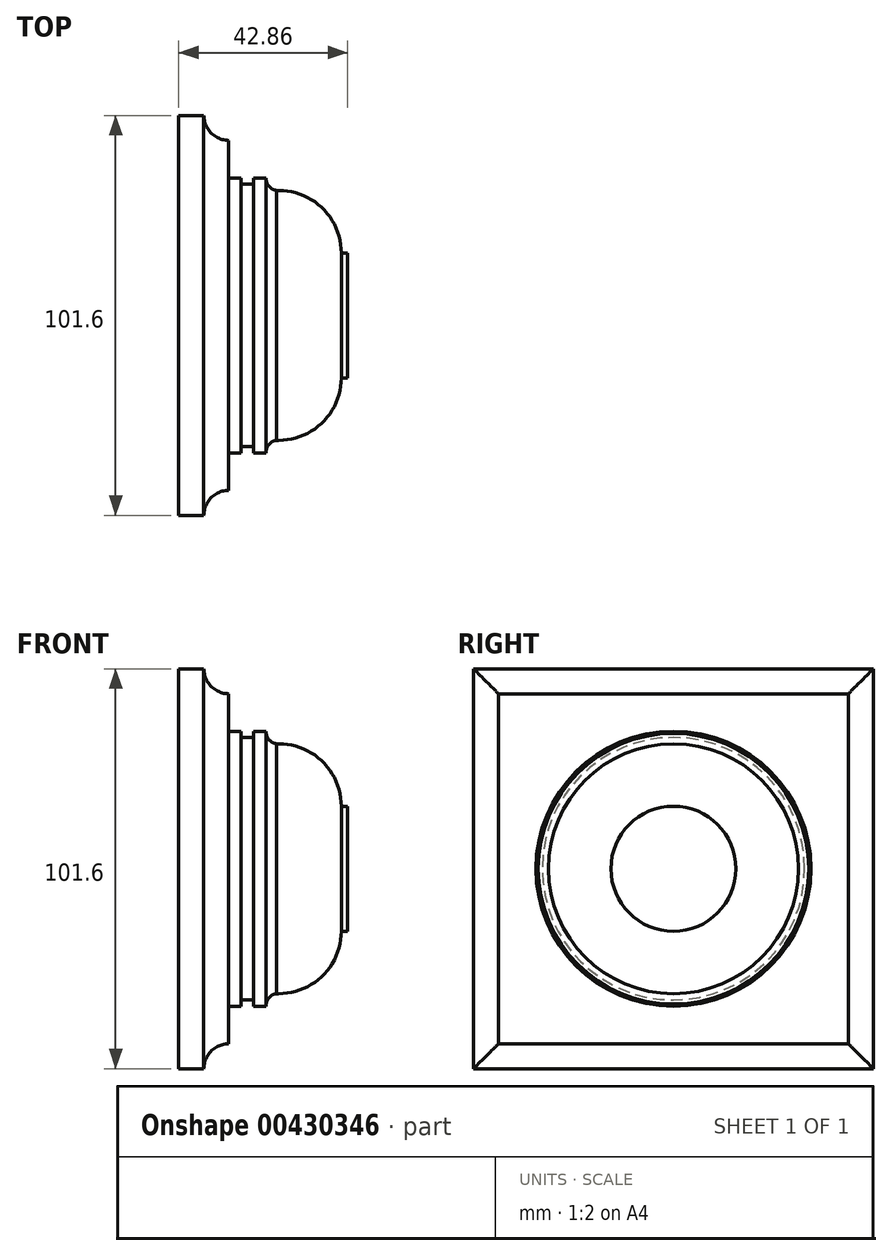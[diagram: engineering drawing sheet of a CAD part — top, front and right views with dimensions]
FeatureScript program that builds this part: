
annotation { "Feature Type Name" : "Feature", "Feature Type Description" : "" }
export const myFeature = defineFeature(function(context is Context, id is Id, definition is map)
    precondition{}
    {
        {
            var Q0;
            Q0=qCreatedBy(makeId("Front.planeOp"),FACE);
            var sketch = newSketch(context, id + "F0", { "sketchPlane" : qUnion([Q0])});
            skLineSegment(sketch, "E0", {"start": v(0, 0) * mm, "end": v(0, 34.93) * mm});
            skLineSegment(sketch, "E1", {"start": v(0, 34.93) * mm, "end": v(3.18, 34.93) * mm});
            skLineSegment(sketch, "E2", {"start": v(3.18, 34.93) * mm, "end": v(3.18, 33.34) * mm});
            skLineSegment(sketch, "E3", {"start": v(3.18, 33.34) * mm, "end": v(6.35, 33.34) * mm});
            skLineSegment(sketch, "E4", {"start": v(6.35, 33.34) * mm, "end": v(6.35, 34.93) * mm});
            skLineSegment(sketch, "E5", {"start": v(6.35, 34.93) * mm, "end": v(9.53, 34.93) * mm});
            skLineSegment(sketch, "E6", {"start": v(9.53, 34.93) * mm, "end": v(9.53, 34.36) * mm});
            skLineSegment(sketch, "E7", {"start": v(12.14, 31.75) * mm, "end": v(12.7, 31.75) * mm});
            skLineSegment(sketch, "E8", {"start": v(12.7, 31.75) * mm, "end": v(12.7, 31.75) * mm});
            skLineSegment(sketch, "E9", {"start": v(28.58, 15.88) * mm, "end": v(28.58, 15.88) * mm});
            skPoint(sketch, "E10.visualSharp", {"position": v(28.58, 31.75) * mm});
            skArc(sketch, "E10.filletArc", {"start": v(28.58, 15.88) * mm, "mid": v(23.93, 27.1) * mm, "end": v(12.7, 31.75) * mm});
            skArc(sketch, "E11", {"start": v(9.53, 34.93) * mm, "mid": v(10.36, 32.59) * mm, "end": v(12.7, 31.75) * mm});
            skPoint(sketch, "E11.third.point", {"position": v(15.1, 35.76) * mm});
            skLineSegment(sketch, "E12", {"start": v(28.58, 15.88) * mm, "end": v(30.16, 15.88) * mm});
            skLineSegment(sketch, "E13", {"start": v(30.16, 15.88) * mm, "end": v(30.16, 0) * mm});
            skLineSegment(sketch, "E14", {"start": v(30.16, 0) * mm, "end": v(0, 0) * mm});
            skSolve(sketch);
        }
        {
            var Q0;
            Q0=qSketchRegion(id+"F0",true);
            var Q1;
            Q1=sQuery(id+"F0.wireOp",EDGE,"E14");
            revolve(context, id + "F1", {"entities" : qUnion([Q0]), "axis" : qUnion([Q1]), "revolveType" : RevolveType.FULL});
        }
        {
            var Q0;
            Q0=qCreatedBy(makeId("Right.planeOp"),FACE);
            var sketch = newSketch(context, id + "F2", { "sketchPlane" : qUnion([Q0])});
            skLineSegment(sketch, "E15.bottom", {"start": v(-50.8, 50.8) * mm, "end": v(50.8, 50.8) * mm});
            skLineSegment(sketch, "E15.top", {"start": v(-50.8, -50.8) * mm, "end": v(50.8, -50.8) * mm});
            skLineSegment(sketch, "E15.left", {"start": v(-50.8, 50.8) * mm, "end": v(-50.8, -50.8) * mm});
            skLineSegment(sketch, "E15.right", {"start": v(50.8, 50.8) * mm, "end": v(50.8, -50.8) * mm});
            skLineSegment(sketch, "E16", {"start": v(0, 0) * mm, "end": v(0, 50.8) * mm, "construction": true});
            skLineSegment(sketch, "E17", {"start": v(0, 0) * mm, "end": v(-50.8, 0) * mm, "construction": true});
            skLineSegment(sketch, "E18", {"start": v(0, 0) * mm, "end": v(50.8, 0) * mm});
            skSolve(sketch);
        }
        {
            var Q0;
            Q0=qSketchRegion(id+"F2",true);
            extrude(context, id + "F3", {"entities" : qUnion([Q0]), "operationType" : NewBodyOperationType.ADD, "oppositeDirection" : true, "depth" : 12.7 * mm});
        }
        {
            var Q0;
            Q0=makeQuery(id+"F3.opExtrude","SWEPT_FACE",FACE,{"disambiguationData":[OSD([sQuery(id+"F2.wireOp",EDGE,"E15.left")])]});
            var sketch = newSketch(context, id + "F4", { "sketchPlane" : qUnion([Q0])});
            skCircle(sketch, "E19", {"center": v(0, 50.8) * mm, "radius": 6.35 * mm});
            skSolve(sketch);
        }
        {
            var Q0;
            Q0=qSketchRegion(id+"F4",true);
            var Q1;
            Q1=makeQuery(id+"F3.opExtrude","CAP_EDGE",EDGE,{"disambiguationData":[OSD([sQuery(id+"F2.wireOp",EDGE,"E15.bottom")])],"isStart":true});
            var Q2;
            Q2=makeQuery(id+"F3.opExtrude","CAP_EDGE",EDGE,{"disambiguationData":[OSD([sQuery(id+"F2.wireOp",EDGE,"E15.right")])],"isStart":true});
            var Q3;
            Q3=makeQuery(id+"F3.opExtrude","CAP_EDGE",EDGE,{"disambiguationData":[OSD([sQuery(id+"F2.wireOp",EDGE,"E15.top")])],"isStart":true});
            var Q4;
            Q4=makeQuery(id+"F3.opExtrude","CAP_EDGE",EDGE,{"disambiguationData":[OSD([sQuery(id+"F2.wireOp",EDGE,"E15.left")])],"isStart":true});
            sweep(context, id + "F5", {"operationType" : NewBodyOperationType.REMOVE, "profiles" : qUnion([Q0]), "path" : qUnion([Q1, Q2, Q3, Q4])});
        }
    });
